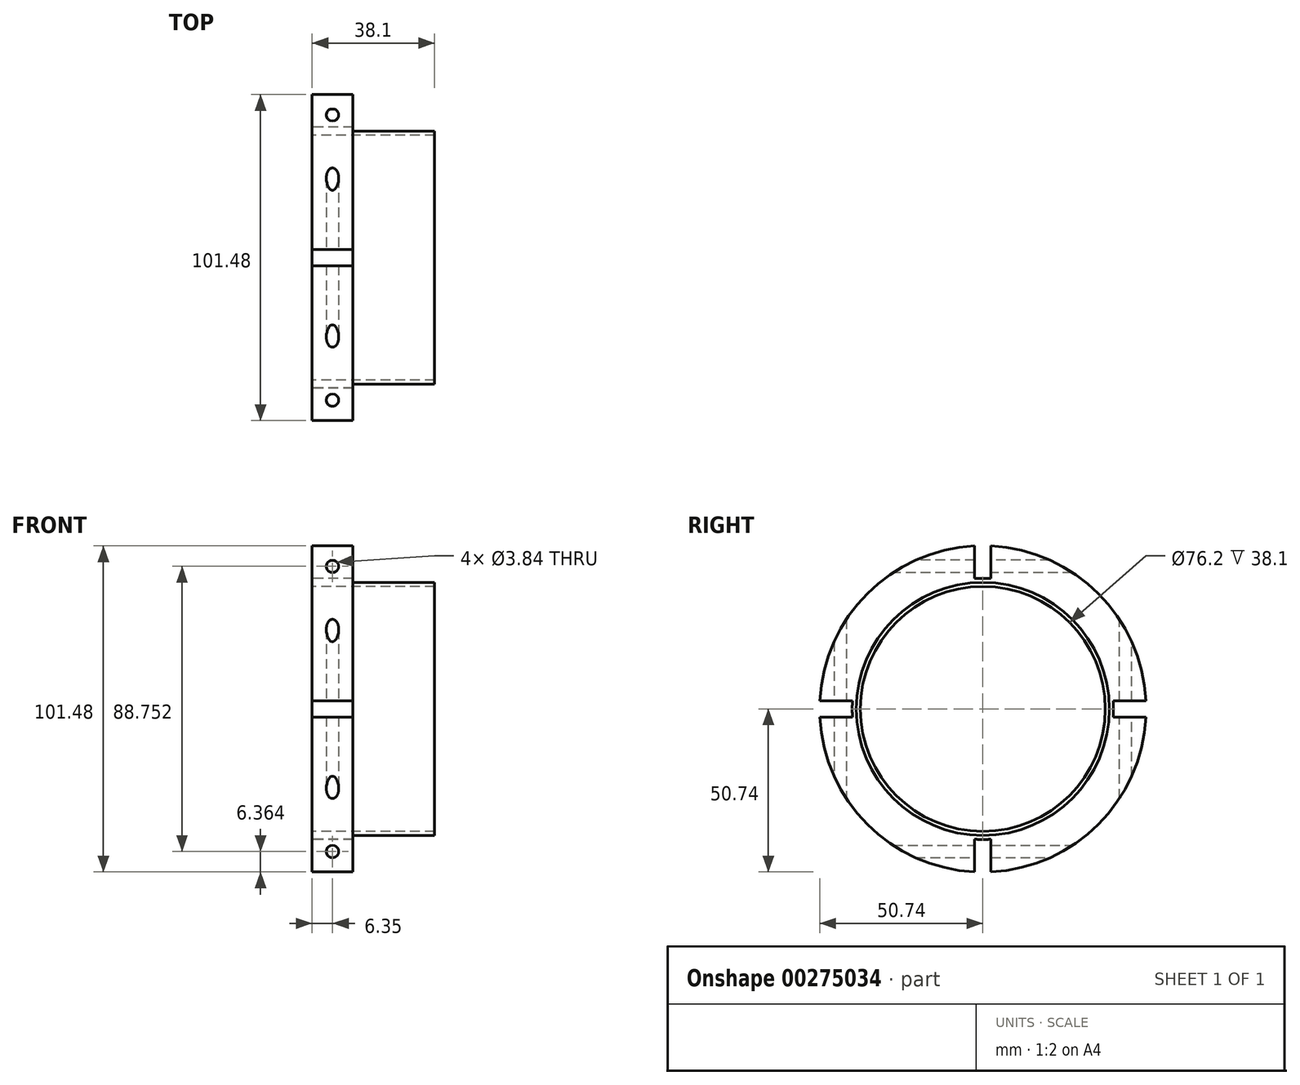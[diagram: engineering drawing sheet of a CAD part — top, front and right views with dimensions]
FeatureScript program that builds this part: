
annotation { "Feature Type Name" : "Feature", "Feature Type Description" : "" }
export const myFeature = defineFeature(function(context is Context, id is Id, definition is map)
    precondition{}
    {
        {
            var Q0;
            Q0=qCreatedBy(makeId("Right.planeOp"),FACE);
            var sketch = newSketch(context, id + "F0", { "sketchPlane" : qUnion([Q0])});
            skCircle(sketch, "E0", {"center": v(0, 0) * mm, "radius": 38.1 * mm});
            skCircle(sketch, "E1", {"center": v(0, 0) * mm, "radius": 50.8 * mm});
            skSolve(sketch);
        }
        {
            var Q0;
            Q0 = qSketchRegion(id + "F0", true);
            extrude(context, id + "F1", {"entities" : qUnion([Q0]), "endBound" : BoundingType.SYMMETRIC, "depth" : 38.1 * mm});
        }
        {
            var Q0;
            Q0=makeQuery(id+"F1.opExtrude","CAP_FACE",FACE,{"disambiguationData":[OSD([sQuery(id+"F0.wireOp",EDGE,"E0"),sQuery(id+"F0.wireOp",EDGE,"E1")])],"isStart":false});
            var sketch = newSketch(context, id + "F2", { "sketchPlane" : qUnion([Q0])});
            skCircle(sketch, "E2", {"center": v(0, 0) * mm, "radius": 39.37 * mm});
            skCircle(sketch, "E3", {"center": v(0, 0) * mm, "radius": 50.8 * mm});
            skSolve(sketch);
        }
        {
            var Q0;
            Q0 = qSketchRegion(id + "F2", true);
            extrude(context, id + "F3", {"entities" : qUnion([Q0]), "operationType" : NewBodyOperationType.REMOVE, "oppositeDirection" : true, "depth" : 25.4 * mm});
        }
        {
            var Q0;
            Q0=makeQuery(id+"F1.opExtrude","CAP_FACE",FACE,{"disambiguationData":[OSD([sQuery(id+"F0.wireOp",EDGE,"E0"),sQuery(id+"F0.wireOp",EDGE,"E1")])],"isStart":true});
            var sketch = newSketch(context, id + "F4", { "sketchPlane" : qUnion([Q0])});
            skPoint(sketch, "E4.middle", {"position": v(42.85, 0) * mm});
            skPoint(sketch, "E5.endSnap0", {"position": v(41.85, 5.72) * mm});
            skPoint(sketch, "E4.right.start.orphan", {"position": v(15.5, 5.72) * mm});
            skPoint(sketch, "E4.top.end.orphan", {"position": v(17.5, -5.72) * mm});
            skPoint(sketch, "E4.left.end.orphan", {"position": v(70.2, -5.72) * mm});
            skPoint(sketch, "E4.bottom.start.orphan", {"position": v(68.2, 5.72) * mm});
            skLineSegment(sketch, "E6.bottom", {"start": v(52.73, -2.54) * mm, "end": v(40.56, -2.54) * mm});
            skLineSegment(sketch, "E6.top", {"start": v(52.73, 2.54) * mm, "end": v(40.56, 2.54) * mm});
            skLineSegment(sketch, "E6.left", {"start": v(52.73, -2.54) * mm, "end": v(52.73, 2.54) * mm});
            skLineSegment(sketch, "E7.bottom", {"start": v(-40.56, -2.54) * mm, "end": v(-59.67, -2.54) * mm});
            skLineSegment(sketch, "E7.top", {"start": v(-40.56, 2.54) * mm, "end": v(-59.67, 2.54) * mm});
            skLineSegment(sketch, "E7.right", {"start": v(-59.67, -2.54) * mm, "end": v(-59.67, 2.54) * mm});
            skPoint(sketch, "E7.middle", {"position": v(-44.4, 0) * mm});
            skLineSegment(sketch, "E8.bottom", {"start": v(2.54, -60.95) * mm, "end": v(-2.54, -60.95) * mm});
            skLineSegment(sketch, "E8.left", {"start": v(2.54, -60.95) * mm, "end": v(2.54, -40.56) * mm});
            skLineSegment(sketch, "E8.right", {"start": v(-2.54, -60.95) * mm, "end": v(-2.54, -40.56) * mm});
            skPoint(sketch, "E8.middle", {"position": v(0, -44.4) * mm});
            skLineSegment(sketch, "E9.top", {"start": v(2.54, 60.43) * mm, "end": v(-2.54, 60.43) * mm});
            skLineSegment(sketch, "E9.left", {"start": v(2.54, 40.56) * mm, "end": v(2.54, 60.43) * mm});
            skLineSegment(sketch, "E9.right", {"start": v(-2.54, 40.56) * mm, "end": v(-2.54, 60.43) * mm});
            skPoint(sketch, "E9.middle", {"position": v(0, 44.4) * mm});
            skArc(sketch, "E10", {"start": v(-2.54, -40.56) * mm, "mid": v(0, -40.64) * mm, "end": v(2.54, -40.56) * mm});
            skPoint(sketch, "E7.left.end.orphan", {"position": v(-29.11, 2.54) * mm});
            skPoint(sketch, "E7.left.start.orphan", {"position": v(-29.11, -2.54) * mm});
            skArc(sketch, "E11.trimOffspring", {"start": v(-40.56, 2.54) * mm, "mid": v(-40.64, 0) * mm, "end": v(-40.56, -2.54) * mm});
            skPoint(sketch, "E6.right.end.orphan", {"position": v(32.98, 2.54) * mm});
            skPoint(sketch, "E6.right.start.orphan", {"position": v(32.98, -2.54) * mm});
            skArc(sketch, "E12.trimOffspring", {"start": v(40.56, -2.54) * mm, "mid": v(40.64, 0) * mm, "end": v(40.56, 2.54) * mm});
            skPoint(sketch, "E8.top.end.orphan", {"position": v(-2.54, -27.84) * mm});
            skPoint(sketch, "E8.top.start.orphan", {"position": v(2.54, -27.84) * mm});
            skArc(sketch, "E13.trimOffspring", {"start": v(2.54, 40.56) * mm, "mid": v(0, 40.64) * mm, "end": v(-2.54, 40.56) * mm});
            skPoint(sketch, "E14.orphan", {"position": v(2.54, 28.35) * mm});
            skPoint(sketch, "E15.orphan", {"position": v(-2.54, 28.35) * mm});
            skSolve(sketch);
        }
        {
            var Q0;
            Q0 = qSketchRegion(id + "F4", true);
            extrude(context, id + "F5", {"entities" : qUnion([Q0]), "operationType" : NewBodyOperationType.REMOVE, "oppositeDirection" : true, "depth" : 12.7 * mm});
        }
        {
            var Q0;
            Q0 = qSketchRegion(id + "F4", true);
            extrude(context, id + "F6", {"entities" : qUnion([Q0]), "operationType" : NewBodyOperationType.REMOVE, "oppositeDirection" : true, "depth" : 12.7 * mm});
        }
        {
            var Q0;
            Q0=makeQuery(id+"F5.boolean.opBoolean","COPY",FACE,{"derivedFrom":makeQuery(id+"F5.opExtrude","SWEPT_FACE",FACE,{"disambiguationData":[OSD([sQuery(id+"F4.wireOp",EDGE,"E6.top")])]})});
            var sketch = newSketch(context, id + "F7", { "sketchPlane" : qUnion([Q0])});
            skCircle(sketch, "E16", {"center": v(-12.7, 44.38) * mm, "radius": 1.92 * mm});
            skSolve(sketch);
        }
        {
            var Q0;
            Q0 = qSketchRegion(id + "F7", true);
            extrude(context, id + "F8", {"entities" : qUnion([Q0]), "operationType" : NewBodyOperationType.REMOVE, "endBound" : BoundingType.SYMMETRIC, "oppositeDirection" : true, "depth" : 63.5 * mm});
        }
        {
            var Q0;
            Q0=makeQuery(id+"F5.boolean.opBoolean","COPY",FACE,{"derivedFrom":makeQuery(id+"F5.opExtrude","SWEPT_FACE",FACE,{"disambiguationData":[OSD([sQuery(id+"F4.wireOp",EDGE,"E9.right")])]})});
            var sketch = newSketch(context, id + "F9", { "sketchPlane" : qUnion([Q0])});
            skCircle(sketch, "E17", {"center": v(-12.7, 44.38) * mm, "radius": 1.92 * mm});
            skSolve(sketch);
        }
        {
            var Q0;
            Q0 = qSketchRegion(id + "F9", true);
            extrude(context, id + "F10", {"entities" : qUnion([Q0]), "operationType" : NewBodyOperationType.REMOVE, "endBound" : BoundingType.SYMMETRIC, "oppositeDirection" : true, "depth" : 63.5 * mm});
        }
        {
            var Q0;
            Q0=makeQuery(id+"F5.boolean.opBoolean","COPY",FACE,{"derivedFrom":makeQuery(id+"F5.opExtrude","SWEPT_FACE",FACE,{"disambiguationData":[OSD([sQuery(id+"F4.wireOp",EDGE,"E7.bottom")])]})});
            var sketch = newSketch(context, id + "F11", { "sketchPlane" : qUnion([Q0])});
            skCircle(sketch, "E18", {"center": v(-12.7, 44.38) * mm, "radius": 1.92 * mm});
            skSolve(sketch);
        }
        {
            var Q0;
            Q0 = qSketchRegion(id + "F11", true);
            extrude(context, id + "F12", {"entities" : qUnion([Q0]), "operationType" : NewBodyOperationType.REMOVE, "endBound" : BoundingType.SYMMETRIC, "oppositeDirection" : true, "depth" : 63.5 * mm});
        }
        {
            var Q0;
            Q0=makeQuery(id+"F5.boolean.opBoolean","COPY",FACE,{"derivedFrom":makeQuery(id+"F5.opExtrude","SWEPT_FACE",FACE,{"disambiguationData":[OSD([sQuery(id+"F4.wireOp",EDGE,"E8.left")])]})});
            var sketch = newSketch(context, id + "F13", { "sketchPlane" : qUnion([Q0])});
            skCircle(sketch, "E19", {"center": v(12.7, -44.38) * mm, "radius": 1.92 * mm});
            skSolve(sketch);
        }
        {
            var Q0;
            Q0 = qSketchRegion(id + "F13", true);
            extrude(context, id + "F14", {"entities" : qUnion([Q0]), "operationType" : NewBodyOperationType.REMOVE, "endBound" : BoundingType.SYMMETRIC, "oppositeDirection" : true, "depth" : 63.5 * mm});
        }
    });
